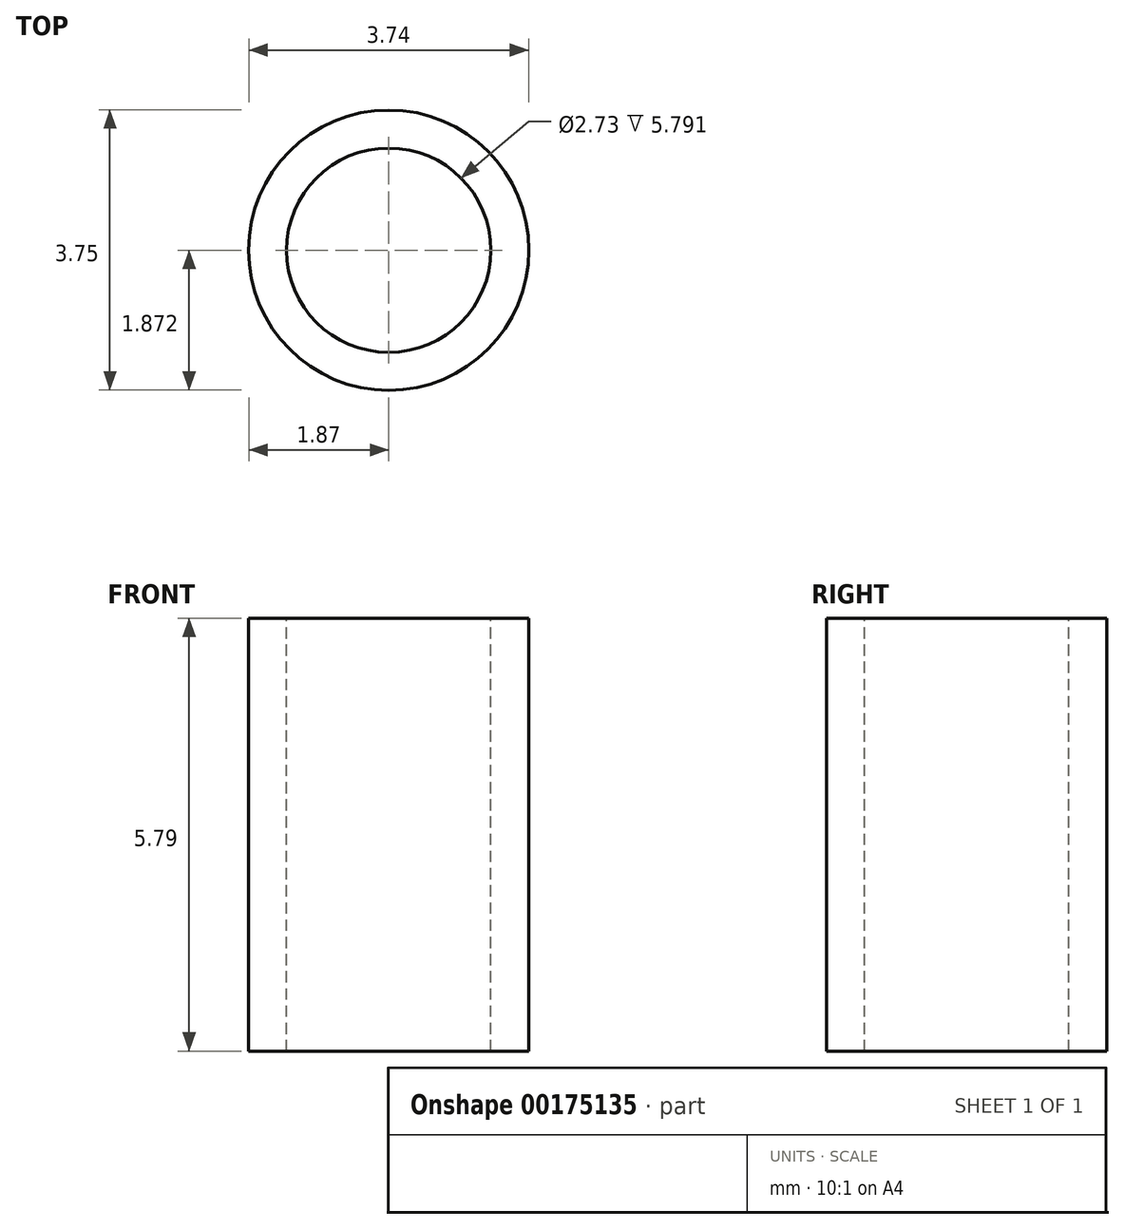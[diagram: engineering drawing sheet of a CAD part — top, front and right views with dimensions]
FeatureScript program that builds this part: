
annotation { "Feature Type Name" : "Feature", "Feature Type Description" : "" }
export const myFeature = defineFeature(function(context is Context, id is Id, definition is map)
    precondition{}
    {
        {
            var Q0;
            Q0=qCreatedBy(makeId("Top.planeOp"),FACE);
            var sketch = newSketch(context, id + "F0", { "sketchPlane" : qUnion([Q0])});
            skLineSegment(sketch, "E0.bottom", {"start": v(5, 3.4) * mm, "end": v(-5, 3.4) * mm});
            skLineSegment(sketch, "E0.top", {"start": v(5, -3.4) * mm, "end": v(-5, -3.4) * mm});
            skLineSegment(sketch, "E0.left", {"start": v(5, 3.4) * mm, "end": v(5, -3.4) * mm});
            skLineSegment(sketch, "E0.right", {"start": v(-5, 3.4) * mm, "end": v(-5, -3.4) * mm});
            skPoint(sketch, "E0.middle", {"position": v(0, 0) * mm});
            skSolve(sketch);
        }
        {
            var Q0;
            Q0=makeQuery(id+"F0.imprint","IMPRINT",FACE,{"disambiguationData":[TD([[makeQuery(id+"F0.imprint","IMPRINT",EDGE,{"derivedFrom":sQuery(id+"F0.wireOp",EDGE,"E0.bottom")}),1.0]])]});
            extrude(context, id + "F1", {"entities" : qUnion([Q0]), "depth" : 5 * mm});
        }
        {
            var Q0;
            Q0=makeQuery(id+"F1.opExtrude","CAP_FACE",FACE,{"disambiguationData":[OSD([sQuery(id+"F0.wireOp",EDGE,"E0.bottom"),sQuery(id+"F0.wireOp",EDGE,"E0.top"),sQuery(id+"F0.wireOp",EDGE,"E0.left"),sQuery(id+"F0.wireOp",EDGE,"E0.right")])],"isStart":false});
            var sketch = newSketch(context, id + "F2", { "sketchPlane" : qUnion([Q0])});
            skLineSegment(sketch, "E1.bottom", {"start": v(-1.98, -3.4) * mm, "end": v(-5, -3.4) * mm});
            skLineSegment(sketch, "E1.top", {"start": v(-1.98, 6.03) * mm, "end": v(-5, 6.03) * mm});
            skLineSegment(sketch, "E1.left", {"start": v(-1.98, -3.4) * mm, "end": v(-1.98, 6.03) * mm});
            skLineSegment(sketch, "E1.right", {"start": v(-5, -3.4) * mm, "end": v(-5, 6.03) * mm});
            skSolve(sketch);
        }
        {
            var Q0;
            {var subQ0=sQuery(id+"F2.wireOp",EDGE,"E1.bottom");Q0=makeQuery(id+"F2.imprint","IMPRINT",FACE,{"disambiguationData":[TD([[makeQuery(id+"F2.imprint","IMPRINT",EDGE,{"derivedFrom":subQ0}),-1.0]])]});}
            var Q1;
            {var subQ0=sQuery(id+"F2.wireOp",EDGE,"E1.top");Q1=makeQuery(id+"F2.imprint","IMPRINT",FACE,{"disambiguationData":[TD([[makeQuery(id+"F2.imprint","IMPRINT",EDGE,{"derivedFrom":subQ0}),1.0]])]});}
            var Q2;
            Q2=makeQuery(id+"F1.opExtrude","CAP_FACE",FACE,{"disambiguationData":[OSD([sQuery(id+"F0.wireOp",EDGE,"E0.bottom"),sQuery(id+"F0.wireOp",EDGE,"E0.top"),sQuery(id+"F0.wireOp",EDGE,"E0.left"),sQuery(id+"F0.wireOp",EDGE,"E0.right")])],"isStart":true});
            extrude(context, id + "F3", {"entities" : qUnion([Q0, Q1]), "operationType" : NewBodyOperationType.ADD, "endBound" : BoundingType.UP_TO_SURFACE, "oppositeDirection" : true, "endBoundEntityFace" : qUnion([Q2]), "depth" : 25.4 * mm});
        }
        {
            var Q0;
            Q0=makeQuery(id+"F3.boolean.opBoolean","MERGE",FACE,{"derivedFrom":[makeQuery(id+"F1.opExtrude","CAP_FACE",FACE,{"disambiguationData":[OSD([sQuery(id+"F0.wireOp",EDGE,"E0.bottom"),sQuery(id+"F0.wireOp",EDGE,"E0.top"),sQuery(id+"F0.wireOp",EDGE,"E0.left"),sQuery(id+"F0.wireOp",EDGE,"E0.right")])],"isStart":false}),makeQuery(id+"F3.opExtrude","CAP_FACE",FACE,{"disambiguationData":[OSD([sQuery(id+"F2.wireOp",EDGE,"E1.bottom"),sQuery(id+"F2.wireOp",EDGE,"E1.top"),sQuery(id+"F2.wireOp",EDGE,"E1.left"),sQuery(id+"F2.wireOp",EDGE,"E1.right")])],"isStart":true})]});
            var sketch = newSketch(context, id + "F4", { "sketchPlane" : qUnion([Q0])});
            skCircle(sketch, "E2", {"center": v(3.73, 2.12) * mm, "radius": 2.54 * mm});
            skSolve(sketch);
        }
        {
            var Q0;
            {var subQ0=sQuery(id+"F4.wireOp",EDGE,"E2");var subQ1=makeQuery(id+"F1.opExtrude","CAP_EDGE",EDGE,{"disambiguationData":[OSD([sQuery(id+"F0.wireOp",EDGE,"E0.left")])],"isStart":false});var subQ2=makeQuery(id+"F4.imprint","INTERSECT",VERTEX,{"derivedFrom":[subQ1,subQ0]});Q0=makeQuery(id+"F4.imprint","IMPRINT",FACE,{"disambiguationData":[TD([[makeQuery(id+"F4.imprint","IMPRINT",EDGE,{"disambiguationData":[TD([[subQ2,-1.0]])],"derivedFrom":subQ0}),1.0]])]});}
            var Q1;
            {var subQ0=sQuery(id+"F0.wireOp",EDGE,"E0.right");var subQ1=sQuery(id+"F0.wireOp",EDGE,"E0.left");var subQ2=sQuery(id+"F0.wireOp",EDGE,"E0.top");var subQ3=sQuery(id+"F0.wireOp",EDGE,"E0.bottom");Q1=makeQuery(id+"F3.boolean.opBoolean","MERGE",FACE,{"derivedFrom":[makeQuery(id+"F1.opExtrude","CAP_FACE",FACE,{"disambiguationData":[OSD([subQ3,subQ2,subQ1,subQ0])],"isStart":true}),makeQuery(id+"F3.opExtrude","CAP_FACE",FACE,{"disambiguationData":[OSD([subQ3,subQ2,subQ1,subQ0])],"isStart":false})]});}
            extrude(context, id + "F5", {"entities" : qUnion([Q0]), "operationType" : NewBodyOperationType.ADD, "endBound" : BoundingType.UP_TO_SURFACE, "oppositeDirection" : true, "endBoundEntityFace" : qUnion([Q1]), "depth" : 25.4 * mm});
        }
        {
            var Q0;
            {var subQ0=sQuery(id+"F0.wireOp",EDGE,"E0.left");var subQ1=sQuery(id+"F0.wireOp",EDGE,"E0.bottom");Q0=makeQuery(id+"F5.boolean.opBoolean","MERGE",FACE,{"derivedFrom":[makeQuery(id+"F3.boolean.opBoolean","MERGE",FACE,{"derivedFrom":[makeQuery(id+"F1.opExtrude","CAP_FACE",FACE,{"disambiguationData":[OSD([subQ1,sQuery(id+"F0.wireOp",EDGE,"E0.top"),subQ0,sQuery(id+"F0.wireOp",EDGE,"E0.right")])],"isStart":false}),makeQuery(id+"F3.opExtrude","CAP_FACE",FACE,{"disambiguationData":[OSD([sQuery(id+"F2.wireOp",EDGE,"E1.bottom"),sQuery(id+"F2.wireOp",EDGE,"E1.top"),sQuery(id+"F2.wireOp",EDGE,"E1.left"),sQuery(id+"F2.wireOp",EDGE,"E1.right")])],"isStart":true})]}),makeQuery(id+"F5.opExtrude","CAP_FACE",FACE,{"disambiguationData":[OSD([subQ1,subQ0,sQuery(id+"F4.wireOp",EDGE,"E2")])],"isStart":true})]});}
            extrude(context, id + "F6", {"entities" : qUnion([Q0]), "operationType" : NewBodyOperationType.REMOVE, "oppositeDirection" : true, "depth" : 3.3 * mm});
        }
        {
            var Q0;
            Q0=makeQuery(id+"F6.boolean.opBoolean","COPY",FACE,{"derivedFrom":makeQuery(id+"F6.opExtrude","CAP_FACE",FACE,{"disambiguationData":[OSD([sQuery(id+"F0.wireOp",EDGE,"E0.bottom"),sQuery(id+"F0.wireOp",EDGE,"E0.top"),sQuery(id+"F0.wireOp",EDGE,"E0.left"),sQuery(id+"F0.wireOp",EDGE,"E0.right"),sQuery(id+"F2.wireOp",EDGE,"E1.bottom"),sQuery(id+"F2.wireOp",EDGE,"E1.top"),sQuery(id+"F2.wireOp",EDGE,"E1.left"),sQuery(id+"F2.wireOp",EDGE,"E1.right"),sQuery(id+"F4.wireOp",EDGE,"E2")])],"isStart":false})});
            cPlane(context, id + "F7", {"entities" : qUnion([Q0]), "cplaneType" : CPlaneType.OFFSET, "offset" : 12.7 * mm, "width" : 152.4 * mm, "height" : 152.4 * mm});
        }
        {
            var Q0;
            Q0=qCreatedBy(id+"F7.planeOp",FACE);
            var sketch = newSketch(context, id + "F8", { "sketchPlane" : qUnion([Q0])});
            skArc(sketch, "E3.0", {"start": v(5, -0.08) * mm, "mid": v(5.53, 3.92) * mm, "end": v(1.53, 3.4) * mm, "construction": true});
            skCircle(sketch, "E4", {"center": v(3.73, 2.12) * mm, "radius": 1.87 * mm});
            skSolve(sketch);
        }
        {
            var Q0;
            Q0=makeQuery(id+"F8.imprint","IMPRINT",FACE,{"disambiguationData":[TD([[makeQuery(id+"F8.imprint","IMPRINT",EDGE,{"derivedFrom":sQuery(id+"F8.wireOp",EDGE,"E4")}),1.0]])]});
            extrude(context, id + "F9", {"entities" : qUnion([Q0]), "depth" : 5.8 * mm});
        }
        {
            var Q0;
            Q0=makeQuery(id+"F1.opExtrude","SWEPT_BODY",BODY,{"disambiguationData":[OSD([sQuery(id+"F0.wireOp",EDGE,"E0.bottom"),sQuery(id+"F0.wireOp",EDGE,"E0.top"),sQuery(id+"F0.wireOp",EDGE,"E0.left"),sQuery(id+"F0.wireOp",EDGE,"E0.right")])]});
            deleteBodies(context, id + "F10", {"entities" : qUnion([Q0])});
        }
        {
            var Q0;
            Q0=makeQuery(id+"F9.opExtrude","CAP_FACE",FACE,{"disambiguationData":[OSD([sQuery(id+"F8.wireOp",EDGE,"E4")])],"isStart":false});
            var sketch = newSketch(context, id + "F11", { "sketchPlane" : qUnion([Q0])});
            skCircle(sketch, "E5", {"center": v(3.73, 2.12) * mm, "radius": 1.37 * mm});
            skSolve(sketch);
        }
        {
            var Q0;
            Q0=makeQuery(id+"F11.imprint","IMPRINT",FACE,{"disambiguationData":[TD([[makeQuery(id+"F11.imprint","IMPRINT",EDGE,{"derivedFrom":sQuery(id+"F11.wireOp",EDGE,"E5")}),1.0]])]});
            extrude(context, id + "F12", {"entities" : qUnion([Q0]), "operationType" : NewBodyOperationType.REMOVE, "oppositeDirection" : true, "depth" : 25.4 * mm});
        }
    });
